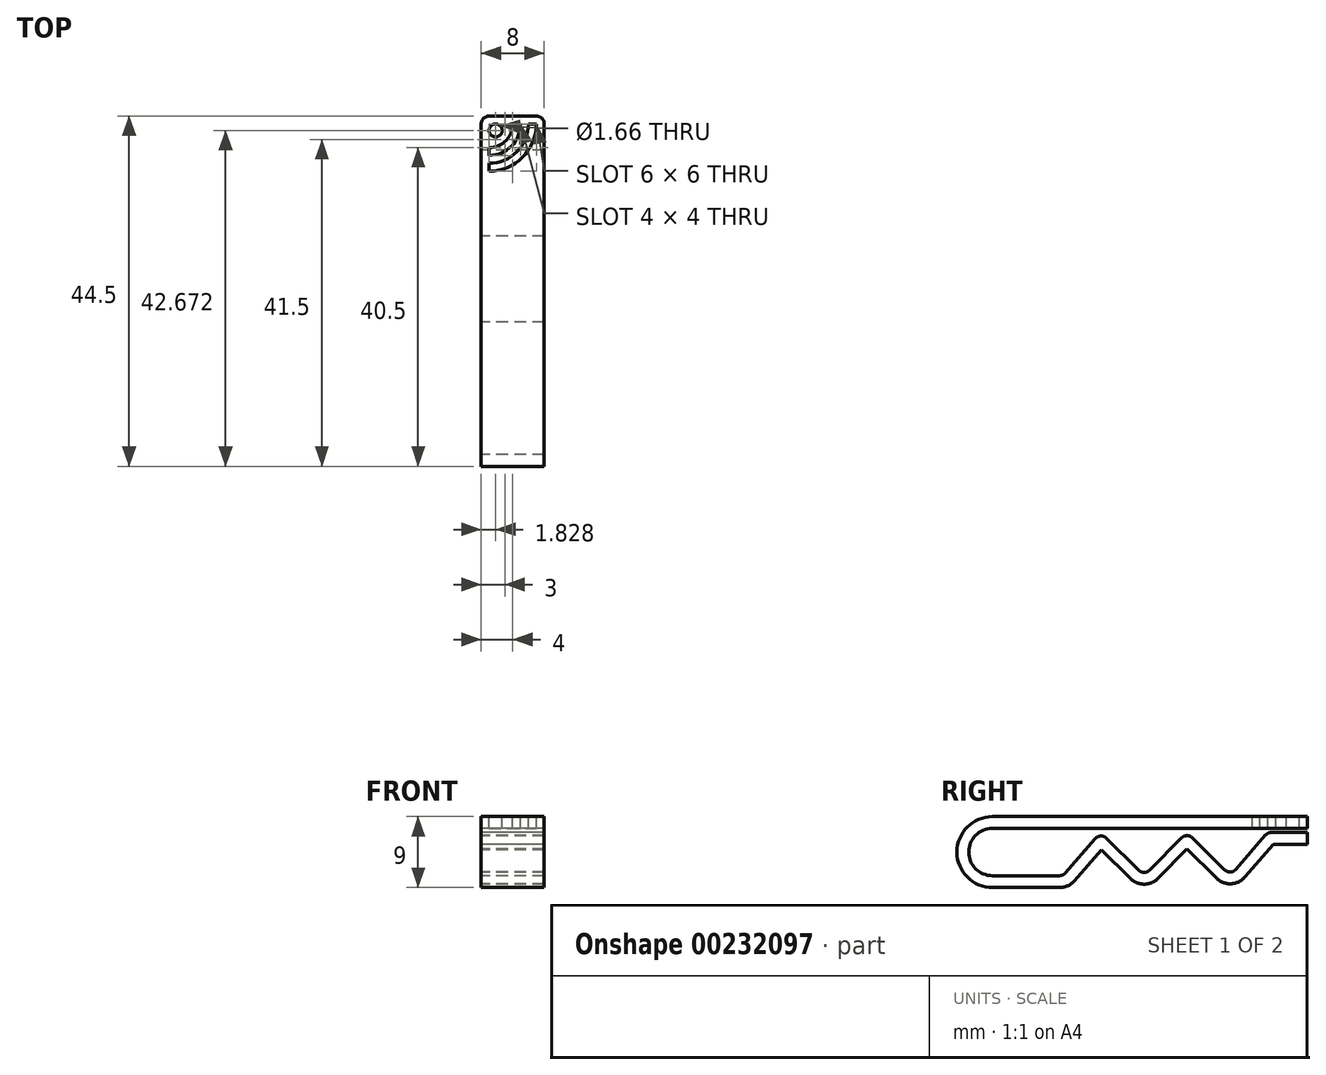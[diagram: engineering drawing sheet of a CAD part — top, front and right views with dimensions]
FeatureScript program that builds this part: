
annotation { "Feature Type Name" : "Feature", "Feature Type Description" : "" }
export const myFeature = defineFeature(function(context is Context, id is Id, definition is map)
    precondition{}
    {
        {
            var Q0;
            Q0=qCreatedBy(makeId("Right.planeOp"),FACE);
            var sketch = newSketch(context, id + "F0", { "sketchPlane" : qUnion([Q0])});
            skArc(sketch, "E0", {"start": v(0, 3) * mm, "mid": v(-3, 0) * mm, "end": v(0, -3) * mm});
            skLineSegment(sketch, "E1", {"start": v(0, -3) * mm, "end": v(8.54, -3) * mm});
            skLineSegment(sketch, "E2", {"start": v(0, 3) * mm, "end": v(40, 3) * mm});
            skLineSegment(sketch, "E3", {"start": v(9.3, -2.65) * mm, "end": v(13.04, 1.69) * mm});
            skLineSegment(sketch, "E4", {"start": v(14.5, 1.74) * mm, "end": v(18.57, -2.3) * mm});
            skLineSegment(sketch, "E5", {"start": v(19.99, -2.29) * mm, "end": v(24.01, 1.79) * mm});
            skLineSegment(sketch, "E6", {"start": v(25.43, 1.8) * mm, "end": v(29.5, -2.24) * mm});
            skLineSegment(sketch, "E7", {"start": v(30.96, -2.19) * mm, "end": v(34.7, 2.15) * mm});
            skLineSegment(sketch, "E8", {"start": v(35.46, 2.5) * mm, "end": v(40, 2.5) * mm});
            skPoint(sketch, "E9.visualSharp", {"position": v(9, -3) * mm});
            skArc(sketch, "E9.filletArc", {"start": v(8.54, -3) * mm, "mid": v(8.96, -2.9) * mm, "end": v(9.3, -2.65) * mm});
            skPoint(sketch, "E10.visualSharp", {"position": v(13.74, 2.5) * mm});
            skArc(sketch, "E10.filletArc", {"start": v(14.5, 1.74) * mm, "mid": v(13.76, 2.03) * mm, "end": v(13.04, 1.69) * mm});
            skPoint(sketch, "E11.visualSharp", {"position": v(19.28, -3) * mm});
            skArc(sketch, "E11.filletArc", {"start": v(18.57, -2.3) * mm, "mid": v(19.28, -2.58) * mm, "end": v(19.99, -2.29) * mm});
            skPoint(sketch, "E12.visualSharp", {"position": v(24.72, 2.5) * mm});
            skArc(sketch, "E12.filletArc", {"start": v(25.43, 1.8) * mm, "mid": v(24.72, 2.08) * mm, "end": v(24.01, 1.79) * mm});
            skPoint(sketch, "E13.visualSharp", {"position": v(30.26, -3) * mm});
            skArc(sketch, "E13.filletArc", {"start": v(29.5, -2.24) * mm, "mid": v(30.24, -2.53) * mm, "end": v(30.96, -2.19) * mm});
            skPoint(sketch, "E14.visualSharp", {"position": v(35, 2.5) * mm});
            skArc(sketch, "E14.filletArc", {"start": v(35.46, 2.5) * mm, "mid": v(35.04, 2.4) * mm, "end": v(34.7, 2.15) * mm});
            skLineSegment(sketch, "E15.0", {"start": v(35.69, 1) * mm, "end": v(40, 1) * mm});
            skLineSegment(sketch, "E15.1", {"start": v(32.1, -3.17) * mm, "end": v(35.69, 1) * mm});
            skArc(sketch, "E15.2", {"start": v(8.54, -4.5) * mm, "mid": v(9.58, -4.27) * mm, "end": v(10.44, -3.63) * mm});
            skLineSegment(sketch, "E15.3", {"start": v(0, -4.5) * mm, "end": v(8.54, -4.5) * mm});
            skArc(sketch, "E15.4", {"start": v(0, 4.5) * mm, "mid": v(-4.5, 0) * mm, "end": v(0, -4.5) * mm});
            skLineSegment(sketch, "E15.5", {"start": v(0, 4.5) * mm, "end": v(40, 4.5) * mm});
            skLineSegment(sketch, "E15.6", {"start": v(10.44, -3.63) * mm, "end": v(13.83, 0.3) * mm});
            skLineSegment(sketch, "E15.7", {"start": v(13.83, 0.3) * mm, "end": v(17.51, -3.36) * mm});
            skArc(sketch, "E15.8", {"start": v(17.51, -3.36) * mm, "mid": v(19.29, -4.08) * mm, "end": v(21.05, -3.34) * mm});
            skLineSegment(sketch, "E15.9", {"start": v(21.05, -3.34) * mm, "end": v(24.73, 0.38) * mm});
            skLineSegment(sketch, "E15.10", {"start": v(24.73, 0.38) * mm, "end": v(28.44, -3.3) * mm});
            skArc(sketch, "E15.11", {"start": v(28.44, -3.3) * mm, "mid": v(30.3, -4.03) * mm, "end": v(32.1, -3.17) * mm});
            skLineSegment(sketch, "E16", {"start": v(40, 4.5) * mm, "end": v(40, 3) * mm});
            skLineSegment(sketch, "E17", {"start": v(40, 1) * mm, "end": v(40, 2.5) * mm});
            skSolve(sketch);
        }
        {
            var Q0;
            Q0=qSketchRegion(id+"F0",true);
            extrude(context, id + "F1", {"entities" : qUnion([Q0]), "depth" : 8 * mm});
        }
        {
            var Q0;
            Q0=makeQuery(id+"F1.opExtrude","SWEPT_FACE",FACE,{"disambiguationData":[OSD([sQuery(id+"F0.wireOp",EDGE,"E15.5")])]});
            var sketch = newSketch(context, id + "F2", { "sketchPlane" : qUnion([Q0])});
            skArc(sketch, "E18", {"start": v(1, 36) * mm, "mid": v(3.12, 36.88) * mm, "end": v(4, 39) * mm});
            skArc(sketch, "E19", {"start": v(1, 34) * mm, "mid": v(4.54, 35.46) * mm, "end": v(6, 39) * mm});
            skLineSegment(sketch, "E20", {"start": v(1, 39) * mm, "end": v(6, 39) * mm, "construction": true});
            skLineSegment(sketch, "E21", {"start": v(1, 39) * mm, "end": v(1, 34) * mm, "construction": true});
            skArc(sketch, "E22.0", {"start": v(1, 33) * mm, "mid": v(5.24, 34.76) * mm, "end": v(7, 39) * mm});
            skArc(sketch, "E23.0", {"start": v(1, 35) * mm, "mid": v(3.83, 36.17) * mm, "end": v(5, 39) * mm});
            skLineSegment(sketch, "E24", {"start": v(7, 39) * mm, "end": v(6, 39) * mm});
            skLineSegment(sketch, "E25", {"start": v(5, 39) * mm, "end": v(4, 39) * mm});
            skLineSegment(sketch, "E26", {"start": v(1, 36) * mm, "end": v(1, 35) * mm});
            skLineSegment(sketch, "E27", {"start": v(1, 34) * mm, "end": v(1, 33) * mm});
            skCircle(sketch, "E28", {"center": v(1.83, 38.17) * mm, "radius": 0.83 * mm});
            skPoint(sketch, "E28.first.point", {"position": v(1.83, 39) * mm});
            skPoint(sketch, "E28.second.point", {"position": v(1, 38.17) * mm});
            skPoint(sketch, "E28.third.point", {"position": v(2.53, 37.74) * mm});
            skSolve(sketch);
        }
        {
            var Q0;
            Q0 = qSketchRegion(id + "F2", true);
            extrude(context, id + "F3", {"entities" : qUnion([Q0]), "operationType" : NewBodyOperationType.REMOVE, "endBound" : BoundingType.UP_TO_NEXT, "oppositeDirection" : true, "depth" : 25 * mm});
        }
        {
            var Q0;
            Q0=makeQuery(id+"F1.opExtrude","CAP_EDGE",EDGE,{"disambiguationData":[OSD([sQuery(id+"F0.wireOp",EDGE,"E16")])],"isStart":false});
            var Q1;
            Q1=makeQuery(id+"F1.opExtrude","CAP_EDGE",EDGE,{"disambiguationData":[OSD([sQuery(id+"F0.wireOp",EDGE,"E17")])],"isStart":false});
            var Q2;
            Q2=makeQuery(id+"F1.opExtrude","CAP_EDGE",EDGE,{"disambiguationData":[OSD([sQuery(id+"F0.wireOp",EDGE,"E17")])],"isStart":true});
            var Q3;
            Q3=makeQuery(id+"F1.opExtrude","CAP_EDGE",EDGE,{"disambiguationData":[OSD([sQuery(id+"F0.wireOp",EDGE,"E16")])],"isStart":true});
            fillet(context, id + "F4", {"entities" : qUnion([Q0, Q1, Q2, Q3]), "radius" : 1 * mm, "tangentPropagation" : true, "allowEdgeOverflow" : false});
        }
    });
